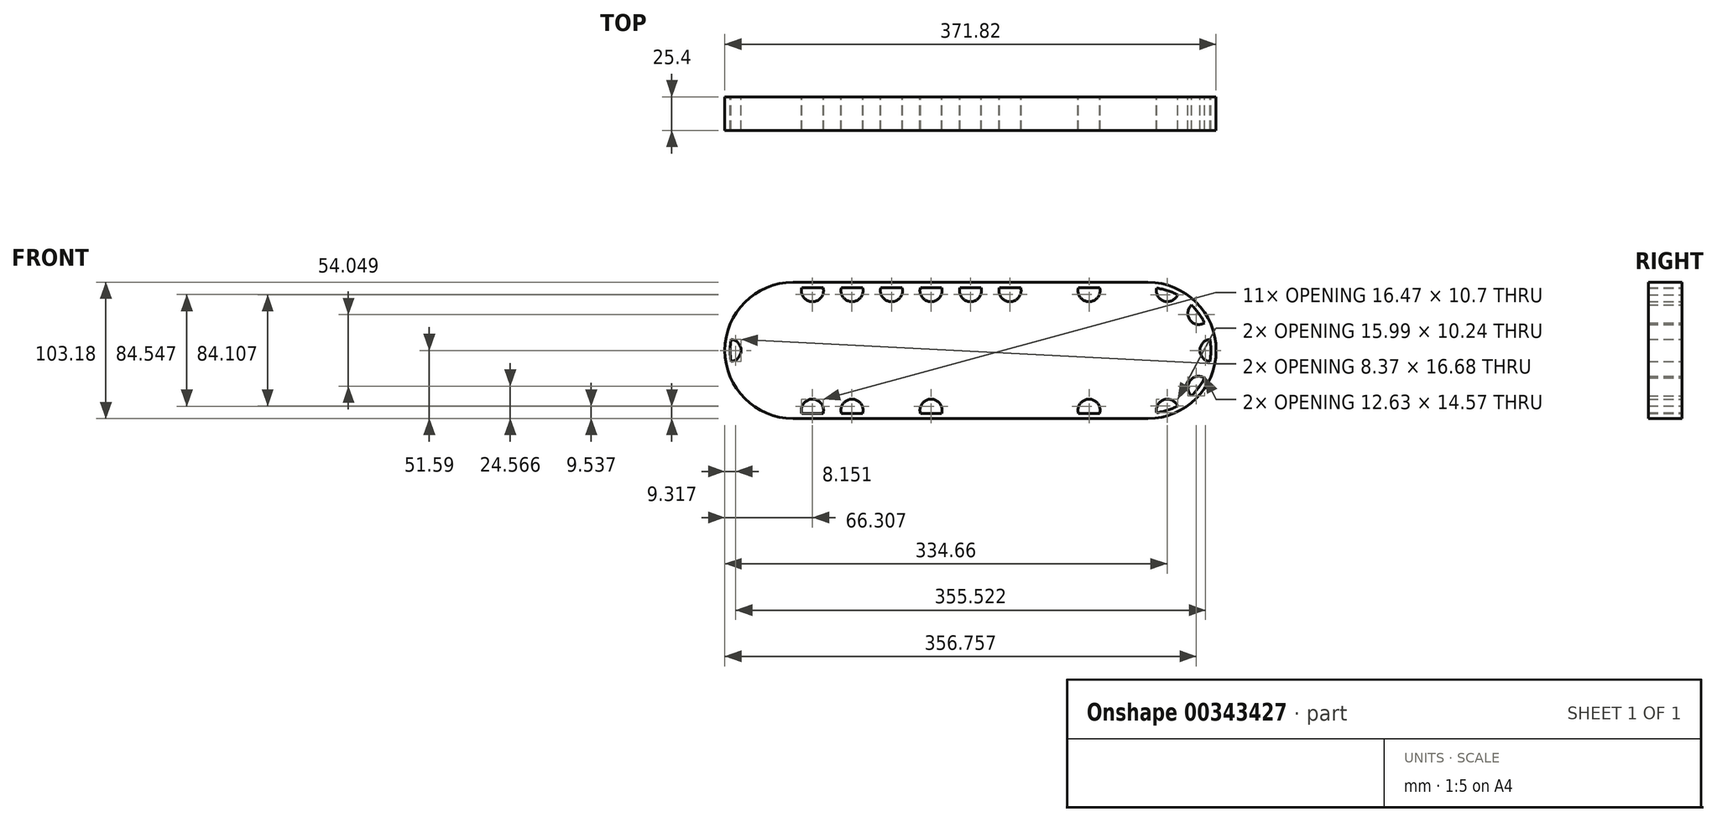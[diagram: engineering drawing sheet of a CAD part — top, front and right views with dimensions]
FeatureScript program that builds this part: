
annotation { "Feature Type Name" : "Feature", "Feature Type Description" : "" }
export const myFeature = defineFeature(function(context is Context, id is Id, definition is map)
    precondition{}
    {
        {
            var Q0;
            Q0=qCreatedBy(makeId("Front.planeOp"),FACE);
            var sketch = newSketch(context, id + "F0", { "sketchPlane" : qUnion([Q0])});
            skCircle(sketch, "E0", {"center": v(0, 0) * mm, "radius": 9.52 * mm});
            skCircle(sketch, "E1", {"center": v(0, 0) * mm, "radius": 15.88 * mm});
            skCircle(sketch, "E2", {"center": v(0, 0) * mm, "radius": 25.4 * mm});
            skCircle(sketch, "E3", {"center": v(0, 0) * mm, "radius": 38.1 * mm});
            skArc(sketch, "E4", {"start": v(5.87, 47.26) * mm, "mid": v(0, 47.63) * mm, "end": v(-5.87, 47.26) * mm});
            skLineSegment(sketch, "E5", {"start": v(-5.87, 47.26) * mm, "end": v(-7.62, 37.33) * mm});
            skLineSegment(sketch, "E6", {"start": v(5.87, 47.26) * mm, "end": v(7.62, 37.33) * mm});
            skLineSegment(sketch, "E7.1.0", {"start": v(-32.53, 34.79) * mm, "end": v(-28.1, 25.72) * mm});
            skArc(sketch, "E7.1.1", {"start": v(-23.03, 41.69) * mm, "mid": v(-28, 38.53) * mm, "end": v(-32.53, 34.79) * mm});
            skLineSegment(sketch, "E7.1.2", {"start": v(-23.03, 41.69) * mm, "end": v(-15.78, 34.68) * mm});
            skLineSegment(sketch, "E7.2.0", {"start": v(-46.76, 9.02) * mm, "end": v(-37.86, 4.29) * mm});
            skArc(sketch, "E7.2.1", {"start": v(-43.14, 20.19) * mm, "mid": v(-45.3, 14.72) * mm, "end": v(-46.76, 9.02) * mm});
            skLineSegment(sketch, "E7.2.2", {"start": v(-43.14, 20.19) * mm, "end": v(-33.15, 18.78) * mm});
            skLineSegment(sketch, "E7.3.0", {"start": v(-43.14, -20.19) * mm, "end": v(-33.15, -18.78) * mm});
            skArc(sketch, "E7.3.1", {"start": v(-46.76, -9.02) * mm, "mid": v(-45.3, -14.72) * mm, "end": v(-43.14, -20.19) * mm});
            skLineSegment(sketch, "E7.3.2", {"start": v(-46.76, -9.02) * mm, "end": v(-37.86, -4.29) * mm});
            skLineSegment(sketch, "E7.4.0", {"start": v(-23.03, -41.69) * mm, "end": v(-15.78, -34.68) * mm});
            skArc(sketch, "E7.4.1", {"start": v(-32.53, -34.79) * mm, "mid": v(-28, -38.53) * mm, "end": v(-23.03, -41.69) * mm});
            skLineSegment(sketch, "E7.4.2", {"start": v(-32.53, -34.79) * mm, "end": v(-28.1, -25.72) * mm});
            skLineSegment(sketch, "E7.5.0", {"start": v(5.87, -47.26) * mm, "end": v(7.62, -37.33) * mm});
            skArc(sketch, "E7.5.1", {"start": v(-5.87, -47.26) * mm, "mid": v(0, -47.63) * mm, "end": v(5.87, -47.26) * mm});
            skLineSegment(sketch, "E7.5.2", {"start": v(-5.87, -47.26) * mm, "end": v(-7.62, -37.33) * mm});
            skLineSegment(sketch, "E7.6.0", {"start": v(32.53, -34.79) * mm, "end": v(28.1, -25.72) * mm});
            skArc(sketch, "E7.6.1", {"start": v(23.03, -41.69) * mm, "mid": v(28, -38.53) * mm, "end": v(32.53, -34.79) * mm});
            skLineSegment(sketch, "E7.6.2", {"start": v(23.03, -41.69) * mm, "end": v(15.78, -34.68) * mm});
            skLineSegment(sketch, "E7.7.0", {"start": v(46.76, -9.02) * mm, "end": v(37.86, -4.29) * mm});
            skArc(sketch, "E7.7.1", {"start": v(43.14, -20.19) * mm, "mid": v(45.3, -14.72) * mm, "end": v(46.76, -9.02) * mm});
            skLineSegment(sketch, "E7.7.2", {"start": v(43.14, -20.19) * mm, "end": v(33.15, -18.78) * mm});
            skLineSegment(sketch, "E7.8.0", {"start": v(43.14, 20.19) * mm, "end": v(33.15, 18.78) * mm});
            skArc(sketch, "E7.8.1", {"start": v(46.76, 9.02) * mm, "mid": v(45.3, 14.72) * mm, "end": v(43.14, 20.19) * mm});
            skLineSegment(sketch, "E7.8.2", {"start": v(46.76, 9.02) * mm, "end": v(37.86, 4.29) * mm});
            skLineSegment(sketch, "E7.9.0", {"start": v(23.03, 41.69) * mm, "end": v(15.78, 34.68) * mm});
            skArc(sketch, "E7.9.1", {"start": v(32.53, 34.79) * mm, "mid": v(28, 38.53) * mm, "end": v(23.03, 41.69) * mm});
            skLineSegment(sketch, "E7.9.2", {"start": v(32.53, 34.79) * mm, "end": v(28.1, 25.72) * mm});
            skLineSegment(sketch, "E8", {"start": v(-3.98, -25.09) * mm, "end": v(-3.98, -15.37) * mm, "construction": true});
            skLineSegment(sketch, "E9", {"start": v(3.98, -15.37) * mm, "end": v(3.98, -25.09) * mm, "construction": true});
            skLineSegment(sketch, "E10.1.0", {"start": v(11.32, 11.13) * mm, "end": v(19.74, 15.99) * mm, "construction": true});
            skLineSegment(sketch, "E10.1.1", {"start": v(23.71, 9.1) * mm, "end": v(15.3, 4.24) * mm, "construction": true});
            skLineSegment(sketch, "E10.2.0", {"start": v(-15.3, 4.24) * mm, "end": v(-23.71, 9.1) * mm, "construction": true});
            skLineSegment(sketch, "E10.2.1", {"start": v(-19.74, 15.99) * mm, "end": v(-11.32, 11.13) * mm, "construction": true});
            skSolve(sketch);
        }
        {
            var Q0;
            Q0=qCreatedBy(makeId("Front.planeOp"),FACE);
            var sketch = newSketch(context, id + "F1", { "sketchPlane" : qUnion([Q0])});
            skArc(sketch, "E11", {"start": v(23.03, 41.69) * mm, "mid": v(-10.34, 46.49) * mm, "end": v(-38.53, 28) * mm});
            skLineSegment(sketch, "E12.0", {"start": v(23.03, 41.69) * mm, "end": v(15.78, 34.68) * mm, "construction": true});
            skLineSegment(sketch, "E12.1", {"start": v(-5.87, 47.26) * mm, "end": v(-7.62, 37.33) * mm, "construction": true});
            skLineSegment(sketch, "E12.2", {"start": v(5.87, 47.26) * mm, "end": v(7.62, 37.33) * mm, "construction": true});
            skLineSegment(sketch, "E12.3", {"start": v(-23.03, 41.69) * mm, "end": v(-15.78, 34.68) * mm, "construction": true});
            skLineSegment(sketch, "E12.4", {"start": v(-32.53, 34.79) * mm, "end": v(-28.1, 25.72) * mm, "construction": true});
            skLineSegment(sketch, "E12.5", {"start": v(-43.14, 20.19) * mm, "end": v(-33.15, 18.78) * mm, "construction": true});
            skLineSegment(sketch, "E12.6", {"start": v(-46.76, 9.02) * mm, "end": v(-37.86, 4.29) * mm, "construction": true});
            skLineSegment(sketch, "E12.7", {"start": v(-46.76, -9.02) * mm, "end": v(-37.86, -4.29) * mm, "construction": true});
            skCircle(sketch, "E13", {"center": v(-14.72, 45.3) * mm, "radius": 8.37 * mm});
            skCircle(sketch, "E14", {"center": v(-38.53, 28) * mm, "radius": 8.37 * mm});
            skCircle(sketch, "E15", {"center": v(-47.62, 0) * mm, "radius": 8.37 * mm});
            skCircle(sketch, "E16", {"center": v(14.72, 45.3) * mm, "radius": 8.37 * mm});
            skArc(sketch, "E17.trimOffspring", {"start": v(-42.84, 20.81) * mm, "mid": v(-45.3, 14.72) * mm, "end": v(-46.89, 8.34) * mm});
            skArc(sketch, "E18.trimOffspring", {"start": v(-47.63, 0) * mm, "mid": v(-24.2, -41.02) * mm, "end": v(23.03, -41.69) * mm});
            skLineSegment(sketch, "E19", {"start": v(-14.72, 45.3) * mm, "end": v(14.72, 45.3) * mm, "construction": true});
            skLineSegment(sketch, "E20", {"start": v(14.72, 45.3) * mm, "end": v(44.62, 45.3) * mm, "construction": true});
            skLineSegment(sketch, "E21", {"start": v(74.52, 45.3) * mm, "end": v(44.62, 45.3) * mm, "construction": true});
            skLineSegment(sketch, "E22", {"start": v(74.52, 45.3) * mm, "end": v(104.42, 45.3) * mm, "construction": true});
            skLineSegment(sketch, "E23", {"start": v(134.32, 45.3) * mm, "end": v(104.42, 45.3) * mm, "construction": true});
            skCircle(sketch, "E24", {"center": v(44.62, 45.3) * mm, "radius": 8.37 * mm});
            skCircle(sketch, "E25", {"center": v(74.52, 45.3) * mm, "radius": 8.37 * mm});
            skCircle(sketch, "E26", {"center": v(104.42, 45.3) * mm, "radius": 8.37 * mm});
            skCircle(sketch, "E27", {"center": v(134.32, 45.3) * mm, "radius": 8.37 * mm});
            skPoint(sketch, "E28", {"position": v(23.09, 45.3) * mm});
            skPoint(sketch, "E29", {"position": v(36.25, 45.3) * mm});
            skLineSegment(sketch, "E30", {"start": v(0, 0) * mm, "end": v(134.32, 0) * mm, "construction": true});
            skLineSegment(sketch, "E31", {"start": v(134.32, 45.3) * mm, "end": v(134.32, 0) * mm, "construction": true});
            skCircle(sketch, "E32.MirrorC", {"center": v(134.32, -45.3) * mm, "radius": 8.37 * mm});
            skCircle(sketch, "E33.MirrorC", {"center": v(104.42, -45.3) * mm, "radius": 8.37 * mm});
            skCircle(sketch, "E34.MirrorC", {"center": v(74.52, -45.3) * mm, "radius": 8.37 * mm});
            skCircle(sketch, "E35.MirrorC", {"center": v(44.62, -45.3) * mm, "radius": 8.37 * mm});
            skCircle(sketch, "E36.MirrorC", {"center": v(14.72, -45.3) * mm, "radius": 8.37 * mm});
            skCircle(sketch, "E37.MirrorC", {"center": v(-14.72, -45.3) * mm, "radius": 8.37 * mm});
            skCircle(sketch, "E38.MirrorC", {"center": v(-38.53, -28) * mm, "radius": 8.37 * mm});
            skCircle(sketch, "E39.MirrorC", {"center": v(164.22, 45.3) * mm, "radius": 8.37 * mm});
            skCircle(sketch, "E40.MirrorC", {"center": v(194.12, 45.3) * mm, "radius": 8.37 * mm});
            skCircle(sketch, "E41.MirrorC", {"center": v(224.03, 45.3) * mm, "radius": 8.37 * mm});
            skCircle(sketch, "E42.MirrorC", {"center": v(253.93, 45.3) * mm, "radius": 8.37 * mm});
            skCircle(sketch, "E43.MirrorC", {"center": v(283.36, 45.3) * mm, "radius": 8.37 * mm});
            skCircle(sketch, "E44.MirrorC", {"center": v(307.17, 28) * mm, "radius": 8.37 * mm});
            skCircle(sketch, "E45.MirrorC", {"center": v(316.27, 0) * mm, "radius": 8.37 * mm});
            skCircle(sketch, "E46.MirrorC", {"center": v(307.17, -28) * mm, "radius": 8.37 * mm});
            skCircle(sketch, "E47.MirrorC", {"center": v(283.36, -45.3) * mm, "radius": 8.37 * mm});
            skCircle(sketch, "E48.MirrorC", {"center": v(253.93, -45.3) * mm, "radius": 8.37 * mm});
            skCircle(sketch, "E49.MirrorC", {"center": v(224.03, -45.3) * mm, "radius": 8.37 * mm});
            skCircle(sketch, "E50.MirrorC", {"center": v(194.12, -45.3) * mm, "radius": 8.37 * mm});
            skCircle(sketch, "E51.MirrorC", {"center": v(164.22, -45.3) * mm, "radius": 8.37 * mm});
            skArc(sketch, "E52", {"start": v(0, 47.63) * mm, "mid": v(-47.63, 0) * mm, "end": v(0, -47.63) * mm});
            skLineSegment(sketch, "E53", {"start": v(0, 47.62) * mm, "end": v(283.02, 47.62) * mm});
            skLineSegment(sketch, "E54", {"start": v(0, -47.62) * mm, "end": v(283.02, -47.62) * mm});
            skSolve(sketch);
        }
        {
            var Q0;
            Q0=qCreatedBy(makeId("Front.planeOp"),FACE);
            var sketch = newSketch(context, id + "F2", { "sketchPlane" : qUnion([Q0])});
            skLineSegment(sketch, "E55.0", {"start": v(0, 47.62) * mm, "end": v(268.64, 47.62) * mm});
            skArc(sketch, "E55.1", {"start": v(0, 47.63) * mm, "mid": v(-47.63, 0) * mm, "end": v(0, -47.63) * mm});
            skLineSegment(sketch, "E55.2", {"start": v(0, -47.62) * mm, "end": v(268.64, -47.62) * mm});
            skLineSegment(sketch, "E55.3", {"start": v(0, 0) * mm, "end": v(134.32, 0) * mm, "construction": true});
            skLineSegment(sketch, "E56.1", {"start": v(134.32, 45.3) * mm, "end": v(134.32, 0) * mm, "construction": true});
            skLineSegment(sketch, "E57.MirrorCS", {"start": v(268.64, 0) * mm, "end": v(134.32, 0) * mm, "construction": true});
            skArc(sketch, "E58", {"start": v(268.64, 47.63) * mm, "mid": v(316.27, 0) * mm, "end": v(268.64, -47.63) * mm});
            skLineSegment(sketch, "E59.0", {"start": v(0, 51.59) * mm, "end": v(128.8, 51.59) * mm});
            skArc(sketch, "E59.1", {"start": v(0, 51.59) * mm, "mid": v(-51.59, 0) * mm, "end": v(0, -51.59) * mm});
            skLineSegment(sketch, "E59.2", {"start": v(0, -51.59) * mm, "end": v(268.64, -51.59) * mm});
            skArc(sketch, "E59.3", {"start": v(268.64, 51.59) * mm, "mid": v(320.23, 0) * mm, "end": v(268.64, -51.59) * mm});
            skArc(sketch, "E60.0", {"start": v(-23.04, 46.15) * mm, "mid": v(-12.13, 37.33) * mm, "end": v(-8.49, 50.88) * mm});
            skArc(sketch, "E60.1", {"start": v(9.2, 51.59) * mm, "mid": v(14.72, 36.92) * mm, "end": v(20.24, 51.59) * mm});
            skArc(sketch, "E60.2", {"start": v(39.1, 51.59) * mm, "mid": v(44.62, 36.92) * mm, "end": v(50.14, 51.59) * mm});
            skArc(sketch, "E60.3", {"start": v(69, 51.59) * mm, "mid": v(74.52, 36.92) * mm, "end": v(80.04, 51.59) * mm});
            skArc(sketch, "E60.4", {"start": v(98.9, 51.59) * mm, "mid": v(104.42, 36.92) * mm, "end": v(109.94, 51.59) * mm});
            skArc(sketch, "E60.5", {"start": v(128.8, 51.59) * mm, "mid": v(134.32, 36.92) * mm, "end": v(139.84, 51.59) * mm});
            skArc(sketch, "E60.6", {"start": v(202.17, 47.62) * mm, "mid": v(191.78, 37.26) * mm, "end": v(188.6, 51.59) * mm});
            skArc(sketch, "E60.7", {"start": v(229.55, 51.59) * mm, "mid": v(224.03, 36.92) * mm, "end": v(218.5, 51.59) * mm});
            skArc(sketch, "E60.8", {"start": v(259.45, 51.59) * mm, "mid": v(253.93, 36.92) * mm, "end": v(248.4, 51.59) * mm});
            skArc(sketch, "E60.9", {"start": v(169.74, 51.59) * mm, "mid": v(164.22, 36.92) * mm, "end": v(158.7, 51.59) * mm});
            skArc(sketch, "E60.10", {"start": v(291.69, 46.15) * mm, "mid": v(280.77, 37.33) * mm, "end": v(277.13, 50.88) * mm});
            skArc(sketch, "E60.11", {"start": v(314.42, 23.8) * mm, "mid": v(300.4, 23.07) * mm, "end": v(305.42, 36.18) * mm});
            skArc(sketch, "E60.12", {"start": v(319.66, -7.65) * mm, "mid": v(307.9, 0) * mm, "end": v(319.66, 7.65) * mm});
            skArc(sketch, "E60.13", {"start": v(314.42, -23.8) * mm, "mid": v(300.4, -23.07) * mm, "end": v(305.42, -36.18) * mm});
            skArc(sketch, "E60.14", {"start": v(291.69, -46.15) * mm, "mid": v(280.77, -37.33) * mm, "end": v(277.13, -50.88) * mm});
            skArc(sketch, "E60.15", {"start": v(259.45, -51.59) * mm, "mid": v(253.93, -36.92) * mm, "end": v(248.4, -51.59) * mm});
            skArc(sketch, "E60.16", {"start": v(229.55, -51.59) * mm, "mid": v(224.03, -36.92) * mm, "end": v(218.5, -51.59) * mm});
            skArc(sketch, "E60.17", {"start": v(199.65, -51.59) * mm, "mid": v(194.12, -36.92) * mm, "end": v(188.6, -51.59) * mm});
            skArc(sketch, "E60.18", {"start": v(169.74, -51.59) * mm, "mid": v(164.22, -36.92) * mm, "end": v(158.7, -51.59) * mm});
            skArc(sketch, "E60.19", {"start": v(128.8, -51.59) * mm, "mid": v(134.32, -36.92) * mm, "end": v(139.84, -51.59) * mm});
            skArc(sketch, "E60.20", {"start": v(98.9, -51.59) * mm, "mid": v(104.42, -36.92) * mm, "end": v(109.94, -51.59) * mm});
            skArc(sketch, "E60.21", {"start": v(69, -51.59) * mm, "mid": v(74.52, -36.92) * mm, "end": v(80.04, -51.59) * mm});
            skArc(sketch, "E60.22", {"start": v(39.1, -51.59) * mm, "mid": v(44.62, -36.92) * mm, "end": v(50.14, -51.59) * mm});
            skArc(sketch, "E60.23", {"start": v(9.2, -51.59) * mm, "mid": v(14.72, -36.92) * mm, "end": v(20.24, -51.59) * mm});
            skArc(sketch, "E60.24", {"start": v(-23.04, -46.15) * mm, "mid": v(-12.13, -37.33) * mm, "end": v(-8.49, -50.88) * mm});
            skArc(sketch, "E60.25", {"start": v(-45.77, -23.8) * mm, "mid": v(-31.76, -23.07) * mm, "end": v(-36.77, -36.18) * mm});
            skArc(sketch, "E60.26", {"start": v(-51.02, -7.65) * mm, "mid": v(-39.25, 0) * mm, "end": v(-51.02, 7.65) * mm});
            skArc(sketch, "E60.27", {"start": v(-45.77, 23.8) * mm, "mid": v(-31.76, 23.07) * mm, "end": v(-36.77, 36.18) * mm});
            skLineSegment(sketch, "E61.trimOffspring", {"start": v(139.84, 51.59) * mm, "end": v(268.64, 51.59) * mm});
            skLineSegment(sketch, "E62", {"start": v(128.8, 51.59) * mm, "end": v(139.84, 51.59) * mm});
            skSolve(sketch);
        }
        {
            var Q0;
            Q0 = qSketchRegion(id + "F2", true);
            var Q1;
            {var subQ0=sQuery(id+"F2.wireOp",EDGE,"E60.26");var subQ1=sQuery(id+"F2.wireOp",EDGE,"E55.1");var subQ2=makeQuery(id+"F2.imprint","INTERSECT",VERTEX,{"disambiguationData":[OD(0.0)],"derivedFrom":[subQ1,subQ0]});Q1=makeQuery(id+"F2.imprint","IMPRINT",FACE,{"disambiguationData":[TD([[makeQuery(id+"F2.imprint","IMPRINT",EDGE,{"disambiguationData":[TD([[subQ2,-1.0]])],"derivedFrom":subQ1}),1.0]])]});}
            var Q2;
            {var subQ0=sQuery(id+"F2.wireOp",EDGE,"E60.25");var subQ1=sQuery(id+"F2.wireOp",EDGE,"E55.1");var subQ2=makeQuery(id+"F2.imprint","INTERSECT",VERTEX,{"disambiguationData":[OD(0.0)],"derivedFrom":[subQ1,subQ0]});Q2=makeQuery(id+"F2.imprint","IMPRINT",FACE,{"disambiguationData":[TD([[makeQuery(id+"F2.imprint","IMPRINT",EDGE,{"disambiguationData":[TD([[subQ2,-1.0]])],"derivedFrom":subQ1}),1.0]])]});}
            var Q3;
            {var subQ0=sQuery(id+"F2.wireOp",EDGE,"E60.23");var subQ1=sQuery(id+"F2.wireOp",EDGE,"E55.2");var subQ2=makeQuery(id+"F2.imprint","INTERSECT",VERTEX,{"disambiguationData":[OD(0.0)],"derivedFrom":[subQ1,subQ0]});Q3=makeQuery(id+"F2.imprint","IMPRINT",FACE,{"disambiguationData":[TD([[makeQuery(id+"F2.imprint","IMPRINT",EDGE,{"disambiguationData":[TD([[subQ2,-1.0]])],"derivedFrom":subQ1}),1.0]])]});}
            var Q4;
            {var subQ0=sQuery(id+"F2.wireOp",EDGE,"E60.22");var subQ1=sQuery(id+"F2.wireOp",EDGE,"E55.2");var subQ2=makeQuery(id+"F2.imprint","INTERSECT",VERTEX,{"disambiguationData":[OD(0.0)],"derivedFrom":[subQ1,subQ0]});Q4=makeQuery(id+"F2.imprint","IMPRINT",FACE,{"disambiguationData":[TD([[makeQuery(id+"F2.imprint","IMPRINT",EDGE,{"disambiguationData":[TD([[subQ2,-1.0]])],"derivedFrom":subQ1}),1.0]])]});}
            var Q5;
            {var subQ0=sQuery(id+"F2.wireOp",EDGE,"E60.21");var subQ1=sQuery(id+"F2.wireOp",EDGE,"E55.2");var subQ2=makeQuery(id+"F2.imprint","INTERSECT",VERTEX,{"disambiguationData":[OD(0.0)],"derivedFrom":[subQ1,subQ0]});Q5=makeQuery(id+"F2.imprint","IMPRINT",FACE,{"disambiguationData":[TD([[makeQuery(id+"F2.imprint","IMPRINT",EDGE,{"disambiguationData":[TD([[subQ2,-1.0]])],"derivedFrom":subQ1}),1.0]])]});}
            var Q6;
            {var subQ0=sQuery(id+"F2.wireOp",EDGE,"E60.20");var subQ1=sQuery(id+"F2.wireOp",EDGE,"E55.2");var subQ2=makeQuery(id+"F2.imprint","INTERSECT",VERTEX,{"disambiguationData":[OD(0.0)],"derivedFrom":[subQ1,subQ0]});Q6=makeQuery(id+"F2.imprint","IMPRINT",FACE,{"disambiguationData":[TD([[makeQuery(id+"F2.imprint","IMPRINT",EDGE,{"disambiguationData":[TD([[subQ2,-1.0]])],"derivedFrom":subQ1}),1.0]])]});}
            var Q7;
            {var subQ0=sQuery(id+"F2.wireOp",EDGE,"E60.19");var subQ1=sQuery(id+"F2.wireOp",EDGE,"E55.2");var subQ2=makeQuery(id+"F2.imprint","INTERSECT",VERTEX,{"disambiguationData":[OD(0.0)],"derivedFrom":[subQ1,subQ0]});Q7=makeQuery(id+"F2.imprint","IMPRINT",FACE,{"disambiguationData":[TD([[makeQuery(id+"F2.imprint","IMPRINT",EDGE,{"disambiguationData":[TD([[subQ2,-1.0]])],"derivedFrom":subQ1}),1.0]])]});}
            var Q8;
            {var subQ0=sQuery(id+"F2.wireOp",EDGE,"E60.18");var subQ1=sQuery(id+"F2.wireOp",EDGE,"E55.2");var subQ2=makeQuery(id+"F2.imprint","INTERSECT",VERTEX,{"disambiguationData":[OD(0.0)],"derivedFrom":[subQ1,subQ0]});Q8=makeQuery(id+"F2.imprint","IMPRINT",FACE,{"disambiguationData":[TD([[makeQuery(id+"F2.imprint","IMPRINT",EDGE,{"disambiguationData":[TD([[subQ2,-1.0]])],"derivedFrom":subQ1}),1.0]])]});}
            var Q9;
            {var subQ0=sQuery(id+"F2.wireOp",EDGE,"E60.24");var subQ1=sQuery(id+"F2.wireOp",EDGE,"E55.1");var subQ2=makeQuery(id+"F2.imprint","INTERSECT",VERTEX,{"disambiguationData":[OD(0.0)],"derivedFrom":[subQ1,subQ0]});Q9=makeQuery(id+"F2.imprint","IMPRINT",FACE,{"disambiguationData":[TD([[makeQuery(id+"F2.imprint","IMPRINT",EDGE,{"disambiguationData":[TD([[subQ2,-1.0]])],"derivedFrom":subQ1}),1.0]])]});}
            var Q10;
            {var subQ0=sQuery(id+"F2.wireOp",EDGE,"E60.17");var subQ1=sQuery(id+"F2.wireOp",EDGE,"E55.2");var subQ2=makeQuery(id+"F2.imprint","INTERSECT",VERTEX,{"disambiguationData":[OD(0.0)],"derivedFrom":[subQ1,subQ0]});Q10=makeQuery(id+"F2.imprint","IMPRINT",FACE,{"disambiguationData":[TD([[makeQuery(id+"F2.imprint","IMPRINT",EDGE,{"disambiguationData":[TD([[subQ2,-1.0]])],"derivedFrom":subQ1}),1.0]])]});}
            var Q11;
            {var subQ0=sQuery(id+"F2.wireOp",EDGE,"E60.16");var subQ1=sQuery(id+"F2.wireOp",EDGE,"E55.2");var subQ2=makeQuery(id+"F2.imprint","INTERSECT",VERTEX,{"disambiguationData":[OD(0.0)],"derivedFrom":[subQ1,subQ0]});Q11=makeQuery(id+"F2.imprint","IMPRINT",FACE,{"disambiguationData":[TD([[makeQuery(id+"F2.imprint","IMPRINT",EDGE,{"disambiguationData":[TD([[subQ2,-1.0]])],"derivedFrom":subQ1}),1.0]])]});}
            var Q12;
            {var subQ0=sQuery(id+"F2.wireOp",EDGE,"E60.15");var subQ1=sQuery(id+"F2.wireOp",EDGE,"E55.2");var subQ2=makeQuery(id+"F2.imprint","INTERSECT",VERTEX,{"disambiguationData":[OD(0.0)],"derivedFrom":[subQ1,subQ0]});Q12=makeQuery(id+"F2.imprint","IMPRINT",FACE,{"disambiguationData":[TD([[makeQuery(id+"F2.imprint","IMPRINT",EDGE,{"disambiguationData":[TD([[subQ2,-1.0]])],"derivedFrom":subQ1}),1.0]])]});}
            var Q13;
            {var subQ0=sQuery(id+"F2.wireOp",EDGE,"E60.14");var subQ1=sQuery(id+"F2.wireOp",EDGE,"E58");var subQ2=makeQuery(id+"F2.imprint","INTERSECT",VERTEX,{"disambiguationData":[OD(0.0)],"derivedFrom":[subQ1,subQ0]});Q13=makeQuery(id+"F2.imprint","IMPRINT",FACE,{"disambiguationData":[TD([[makeQuery(id+"F2.imprint","IMPRINT",EDGE,{"disambiguationData":[TD([[subQ2,-1.0]])],"derivedFrom":subQ1}),-1.0]])]});}
            var Q14;
            {var subQ0=sQuery(id+"F2.wireOp",EDGE,"E60.13");var subQ1=sQuery(id+"F2.wireOp",EDGE,"E58");var subQ2=makeQuery(id+"F2.imprint","INTERSECT",VERTEX,{"disambiguationData":[OD(0.0)],"derivedFrom":[subQ1,subQ0]});Q14=makeQuery(id+"F2.imprint","IMPRINT",FACE,{"disambiguationData":[TD([[makeQuery(id+"F2.imprint","IMPRINT",EDGE,{"disambiguationData":[TD([[subQ2,-1.0]])],"derivedFrom":subQ1}),-1.0]])]});}
            var Q15;
            {var subQ0=sQuery(id+"F2.wireOp",EDGE,"E60.12");var subQ1=sQuery(id+"F2.wireOp",EDGE,"E58");var subQ2=makeQuery(id+"F2.imprint","INTERSECT",VERTEX,{"disambiguationData":[OD(0.0)],"derivedFrom":[subQ1,subQ0]});Q15=makeQuery(id+"F2.imprint","IMPRINT",FACE,{"disambiguationData":[TD([[makeQuery(id+"F2.imprint","IMPRINT",EDGE,{"disambiguationData":[TD([[subQ2,-1.0]])],"derivedFrom":subQ1}),-1.0]])]});}
            var Q16;
            {var subQ0=sQuery(id+"F2.wireOp",EDGE,"E60.11");var subQ1=sQuery(id+"F2.wireOp",EDGE,"E58");var subQ2=makeQuery(id+"F2.imprint","INTERSECT",VERTEX,{"disambiguationData":[OD(0.0)],"derivedFrom":[subQ1,subQ0]});Q16=makeQuery(id+"F2.imprint","IMPRINT",FACE,{"disambiguationData":[TD([[makeQuery(id+"F2.imprint","IMPRINT",EDGE,{"disambiguationData":[TD([[subQ2,-1.0]])],"derivedFrom":subQ1}),-1.0]])]});}
            var Q17;
            {var subQ0=sQuery(id+"F2.wireOp",EDGE,"E60.10");var subQ1=sQuery(id+"F2.wireOp",EDGE,"E58");var subQ2=makeQuery(id+"F2.imprint","INTERSECT",VERTEX,{"disambiguationData":[OD(0.0)],"derivedFrom":[subQ1,subQ0]});Q17=makeQuery(id+"F2.imprint","IMPRINT",FACE,{"disambiguationData":[TD([[makeQuery(id+"F2.imprint","IMPRINT",EDGE,{"disambiguationData":[TD([[subQ2,-1.0]])],"derivedFrom":subQ1}),-1.0]])]});}
            var Q18;
            {var subQ0=sQuery(id+"F2.wireOp",EDGE,"E60.8");var subQ1=sQuery(id+"F2.wireOp",EDGE,"E55.0");var subQ2=makeQuery(id+"F2.imprint","INTERSECT",VERTEX,{"disambiguationData":[OD(0.0)],"derivedFrom":[subQ1,subQ0]});Q18=makeQuery(id+"F2.imprint","IMPRINT",FACE,{"disambiguationData":[TD([[makeQuery(id+"F2.imprint","IMPRINT",EDGE,{"disambiguationData":[TD([[subQ2,-1.0]])],"derivedFrom":subQ1}),-1.0]])]});}
            var Q19;
            {var subQ0=sQuery(id+"F2.wireOp",EDGE,"E60.7");var subQ1=sQuery(id+"F2.wireOp",EDGE,"E55.0");var subQ2=makeQuery(id+"F2.imprint","INTERSECT",VERTEX,{"disambiguationData":[OD(0.0)],"derivedFrom":[subQ1,subQ0]});Q19=makeQuery(id+"F2.imprint","IMPRINT",FACE,{"disambiguationData":[TD([[makeQuery(id+"F2.imprint","IMPRINT",EDGE,{"disambiguationData":[TD([[subQ2,-1.0]])],"derivedFrom":subQ1}),-1.0]])]});}
            var Q20;
            {var subQ0=sQuery(id+"F2.wireOp",EDGE,"E60.6");var subQ1=sQuery(id+"F2.wireOp",EDGE,"E55.0");var subQ2=makeQuery(id+"F2.imprint","INTERSECT",VERTEX,{"disambiguationData":[OD(0.0)],"derivedFrom":[subQ1,subQ0]});Q20=makeQuery(id+"F2.imprint","IMPRINT",FACE,{"disambiguationData":[TD([[makeQuery(id+"F2.imprint","IMPRINT",EDGE,{"disambiguationData":[TD([[subQ2,1.0]])],"derivedFrom":subQ1}),-1.0]])]});}
            var Q21;
            {var subQ0=sQuery(id+"F2.wireOp",EDGE,"E60.9");var subQ1=sQuery(id+"F2.wireOp",EDGE,"E55.0");var subQ2=makeQuery(id+"F2.imprint","INTERSECT",VERTEX,{"disambiguationData":[OD(0.0)],"derivedFrom":[subQ1,subQ0]});Q21=makeQuery(id+"F2.imprint","IMPRINT",FACE,{"disambiguationData":[TD([[makeQuery(id+"F2.imprint","IMPRINT",EDGE,{"disambiguationData":[TD([[subQ2,-1.0]])],"derivedFrom":subQ1}),-1.0]])]});}
            var Q22;
            {var subQ0=sQuery(id+"F2.wireOp",EDGE,"E60.4");var subQ1=sQuery(id+"F2.wireOp",EDGE,"E55.0");var subQ2=makeQuery(id+"F2.imprint","INTERSECT",VERTEX,{"disambiguationData":[OD(0.0)],"derivedFrom":[subQ1,subQ0]});Q22=makeQuery(id+"F2.imprint","IMPRINT",FACE,{"disambiguationData":[TD([[makeQuery(id+"F2.imprint","IMPRINT",EDGE,{"disambiguationData":[TD([[subQ2,-1.0]])],"derivedFrom":subQ1}),-1.0]])]});}
            var Q23;
            {var subQ0=sQuery(id+"F2.wireOp",EDGE,"E60.3");var subQ1=sQuery(id+"F2.wireOp",EDGE,"E55.0");var subQ2=makeQuery(id+"F2.imprint","INTERSECT",VERTEX,{"disambiguationData":[OD(0.0)],"derivedFrom":[subQ1,subQ0]});Q23=makeQuery(id+"F2.imprint","IMPRINT",FACE,{"disambiguationData":[TD([[makeQuery(id+"F2.imprint","IMPRINT",EDGE,{"disambiguationData":[TD([[subQ2,-1.0]])],"derivedFrom":subQ1}),-1.0]])]});}
            var Q24;
            {var subQ0=sQuery(id+"F2.wireOp",EDGE,"E60.2");var subQ1=sQuery(id+"F2.wireOp",EDGE,"E55.0");var subQ2=makeQuery(id+"F2.imprint","INTERSECT",VERTEX,{"disambiguationData":[OD(0.0)],"derivedFrom":[subQ1,subQ0]});Q24=makeQuery(id+"F2.imprint","IMPRINT",FACE,{"disambiguationData":[TD([[makeQuery(id+"F2.imprint","IMPRINT",EDGE,{"disambiguationData":[TD([[subQ2,-1.0]])],"derivedFrom":subQ1}),-1.0]])]});}
            var Q25;
            {var subQ0=sQuery(id+"F2.wireOp",EDGE,"E60.1");var subQ1=sQuery(id+"F2.wireOp",EDGE,"E55.0");var subQ2=makeQuery(id+"F2.imprint","INTERSECT",VERTEX,{"disambiguationData":[OD(0.0)],"derivedFrom":[subQ1,subQ0]});Q25=makeQuery(id+"F2.imprint","IMPRINT",FACE,{"disambiguationData":[TD([[makeQuery(id+"F2.imprint","IMPRINT",EDGE,{"disambiguationData":[TD([[subQ2,-1.0]])],"derivedFrom":subQ1}),-1.0]])]});}
            var Q26;
            {var subQ0=sQuery(id+"F2.wireOp",EDGE,"E60.0");var subQ1=sQuery(id+"F2.wireOp",EDGE,"E55.1");var subQ2=makeQuery(id+"F2.imprint","INTERSECT",VERTEX,{"disambiguationData":[OD(0.0)],"derivedFrom":[subQ1,subQ0]});Q26=makeQuery(id+"F2.imprint","IMPRINT",FACE,{"disambiguationData":[TD([[makeQuery(id+"F2.imprint","IMPRINT",EDGE,{"disambiguationData":[TD([[subQ2,-1.0]])],"derivedFrom":subQ1}),1.0]])]});}
            var Q27;
            {var subQ0=sQuery(id+"F2.wireOp",EDGE,"E60.27");var subQ1=sQuery(id+"F2.wireOp",EDGE,"E55.1");var subQ2=makeQuery(id+"F2.imprint","INTERSECT",VERTEX,{"disambiguationData":[OD(0.0)],"derivedFrom":[subQ1,subQ0]});Q27=makeQuery(id+"F2.imprint","IMPRINT",FACE,{"disambiguationData":[TD([[makeQuery(id+"F2.imprint","IMPRINT",EDGE,{"disambiguationData":[TD([[subQ2,-1.0]])],"derivedFrom":subQ1}),1.0]])]});}
            var Q28;
            {var subQ0=sQuery(id+"F2.wireOp",EDGE,"E60.5");var subQ1=sQuery(id+"F2.wireOp",EDGE,"E55.0");var subQ2=makeQuery(id+"F2.imprint","INTERSECT",VERTEX,{"disambiguationData":[OD(0.0)],"derivedFrom":[subQ1,subQ0]});Q28=makeQuery(id+"F2.imprint","IMPRINT",FACE,{"disambiguationData":[TD([[makeQuery(id+"F2.imprint","IMPRINT",EDGE,{"disambiguationData":[TD([[subQ2,-1.0]])],"derivedFrom":subQ1}),-1.0]])]});}
            extrude(context, id + "F3", {"entities" : qUnion([Q0, Q1, Q2, Q3, Q4, Q5, Q6, Q7, Q8, Q9, Q10, Q11, Q12, Q13, Q14, Q15, Q16, Q17, Q18, Q19, Q20, Q21, Q22, Q23, Q24, Q25, Q26, Q27, Q28]), "depth" : 25.4 * mm});
        }
    });
